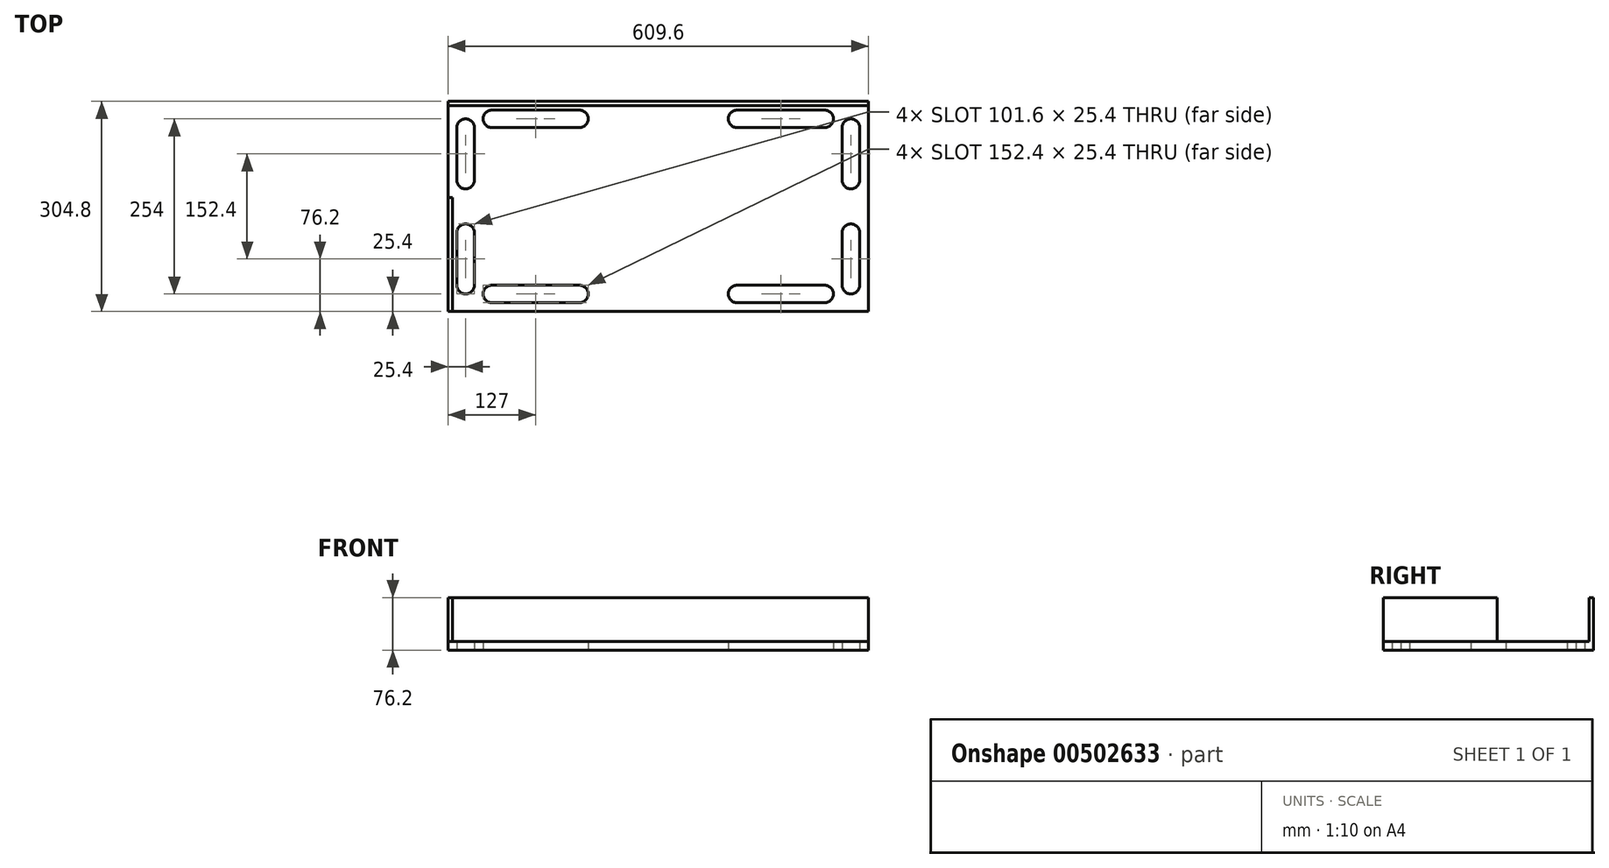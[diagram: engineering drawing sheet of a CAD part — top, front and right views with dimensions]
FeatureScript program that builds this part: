
annotation { "Feature Type Name" : "Feature", "Feature Type Description" : "" }
export const myFeature = defineFeature(function(context is Context, id is Id, definition is map)
    precondition{}
    {
        {
            var Q0;
            Q0=qCreatedBy(makeId("Top.planeOp"),FACE);
            var sketch = newSketch(context, id + "F0", { "sketchPlane" : qUnion([Q0])});
            skLineSegment(sketch, "E0.bottom", {"start": v(0, 0) * mm, "end": v(609.6, 0) * mm});
            skLineSegment(sketch, "E0.top", {"start": v(0, 304.8) * mm, "end": v(609.6, 304.8) * mm});
            skLineSegment(sketch, "E0.left", {"start": v(0, 0) * mm, "end": v(0, 304.8) * mm});
            skLineSegment(sketch, "E0.right", {"start": v(609.6, 0) * mm, "end": v(609.6, 304.8) * mm});
            skLineSegment(sketch, "E1", {"start": v(12.7, 190.5) * mm, "end": v(12.7, 266.7) * mm});
            skLineSegment(sketch, "E2", {"start": v(38.1, 190.5) * mm, "end": v(38.1, 266.7) * mm});
            skArc(sketch, "E3", {"start": v(12.7, 190.5) * mm, "mid": v(25.4, 177.8) * mm, "end": v(38.1, 190.5) * mm});
            skArc(sketch, "E4", {"start": v(38.1, 266.7) * mm, "mid": v(25.4, 279.4) * mm, "end": v(12.7, 266.7) * mm});
            skLineSegment(sketch, "E5", {"start": v(12.7, 38.1) * mm, "end": v(12.7, 114.3) * mm});
            skLineSegment(sketch, "E6", {"start": v(38.1, 38.1) * mm, "end": v(38.1, 114.3) * mm});
            skArc(sketch, "E7", {"start": v(12.7, 38.1) * mm, "mid": v(25.4, 25.4) * mm, "end": v(38.1, 38.1) * mm});
            skArc(sketch, "E8", {"start": v(38.1, 114.3) * mm, "mid": v(25.4, 127) * mm, "end": v(12.7, 114.3) * mm});
            skLineSegment(sketch, "E9", {"start": v(571.5, 190.5) * mm, "end": v(571.5, 266.7) * mm});
            skLineSegment(sketch, "E10", {"start": v(596.9, 190.5) * mm, "end": v(596.9, 266.7) * mm});
            skArc(sketch, "E11", {"start": v(571.5, 190.5) * mm, "mid": v(584.2, 177.8) * mm, "end": v(596.9, 190.5) * mm});
            skArc(sketch, "E12", {"start": v(596.9, 266.7) * mm, "mid": v(584.2, 279.4) * mm, "end": v(571.5, 266.7) * mm});
            skLineSegment(sketch, "E13", {"start": v(571.5, 38.1) * mm, "end": v(571.5, 114.3) * mm});
            skLineSegment(sketch, "E14", {"start": v(596.9, 38.1) * mm, "end": v(596.9, 114.3) * mm});
            skArc(sketch, "E15", {"start": v(571.5, 38.1) * mm, "mid": v(584.2, 25.4) * mm, "end": v(596.9, 38.1) * mm});
            skArc(sketch, "E16", {"start": v(596.9, 114.3) * mm, "mid": v(584.2, 127) * mm, "end": v(571.5, 114.3) * mm});
            skLineSegment(sketch, "E17", {"start": v(190.5, 12.7) * mm, "end": v(63.5, 12.7) * mm});
            skLineSegment(sketch, "E18", {"start": v(190.5, 38.1) * mm, "end": v(63.5, 38.1) * mm});
            skArc(sketch, "E19", {"start": v(190.5, 12.7) * mm, "mid": v(203.2, 25.4) * mm, "end": v(190.5, 38.1) * mm});
            skArc(sketch, "E20", {"start": v(63.5, 38.1) * mm, "mid": v(50.8, 25.4) * mm, "end": v(63.5, 12.7) * mm});
            skLineSegment(sketch, "E21", {"start": v(546.1, 12.7) * mm, "end": v(419.1, 12.7) * mm});
            skLineSegment(sketch, "E22", {"start": v(546.1, 38.1) * mm, "end": v(419.1, 38.1) * mm});
            skArc(sketch, "E23", {"start": v(546.1, 12.7) * mm, "mid": v(558.8, 25.4) * mm, "end": v(546.1, 38.1) * mm});
            skArc(sketch, "E24", {"start": v(419.1, 38.1) * mm, "mid": v(406.4, 25.4) * mm, "end": v(419.1, 12.7) * mm});
            skLineSegment(sketch, "E25", {"start": v(190.5, 266.7) * mm, "end": v(63.5, 266.7) * mm});
            skLineSegment(sketch, "E26", {"start": v(190.5, 292.1) * mm, "end": v(63.5, 292.1) * mm});
            skArc(sketch, "E27", {"start": v(190.5, 266.7) * mm, "mid": v(203.2, 279.4) * mm, "end": v(190.5, 292.1) * mm});
            skArc(sketch, "E28", {"start": v(63.5, 292.1) * mm, "mid": v(50.8, 279.4) * mm, "end": v(63.5, 266.7) * mm});
            skLineSegment(sketch, "E29", {"start": v(546.1, 266.7) * mm, "end": v(419.1, 266.7) * mm});
            skLineSegment(sketch, "E30", {"start": v(546.1, 292.1) * mm, "end": v(419.1, 292.1) * mm});
            skArc(sketch, "E31", {"start": v(546.1, 266.7) * mm, "mid": v(558.8, 279.4) * mm, "end": v(546.1, 292.1) * mm});
            skArc(sketch, "E32", {"start": v(419.1, 292.1) * mm, "mid": v(406.4, 279.4) * mm, "end": v(419.1, 266.7) * mm});
            skSolve(sketch);
        }
        {
            var Q0;
            Q0=makeQuery(id+"F0.imprint","IMPRINT",FACE,{"disambiguationData":[TD([[makeQuery(id+"F0.imprint","IMPRINT",EDGE,{"derivedFrom":sQuery(id+"F0.wireOp",EDGE,"E0.bottom")}),1.0]])]});
            extrude(context, id + "F1", {"entities" : qUnion([Q0]), "depth" : 12.7 * mm});
        }
        {
            var Q0;
            Q0=makeQuery(id+"F1.opExtrude","SWEPT_FACE",FACE,{"disambiguationData":[OSD([sQuery(id+"F0.wireOp",EDGE,"E0.top")])]});
            var sketch = newSketch(context, id + "F2", { "sketchPlane" : qUnion([Q0])});
            skLineSegment(sketch, "E33.bottom", {"start": v(-609.6, 0) * mm, "end": v(0, 0) * mm});
            skLineSegment(sketch, "E33.top", {"start": v(-609.6, 76.2) * mm, "end": v(0, 76.2) * mm});
            skLineSegment(sketch, "E33.left", {"start": v(-609.6, 0) * mm, "end": v(-609.6, 76.2) * mm});
            skLineSegment(sketch, "E33.right", {"start": v(0, 0) * mm, "end": v(0, 76.2) * mm});
            skSolve(sketch);
        }
        {
            var Q0;
            {var subQ0=sQuery(id+"F2.wireOp",EDGE,"E33.top");Q0=makeQuery(id+"F2.imprint","IMPRINT",FACE,{"disambiguationData":[TD([[makeQuery(id+"F2.imprint","IMPRINT",EDGE,{"derivedFrom":subQ0}),-1.0]])]});}
            extrude(context, id + "F3", {"entities" : qUnion([Q0]), "operationType" : NewBodyOperationType.ADD, "oppositeDirection" : true, "depth" : 6.35 * mm});
        }
        {
            var Q0;
            Q0=makeQuery(id+"F3.boolean.opBoolean","MERGE",FACE,{"derivedFrom":[makeQuery(id+"F1.opExtrude","SWEPT_FACE",FACE,{"disambiguationData":[OSD([sQuery(id+"F0.wireOp",EDGE,"E0.left")])]}),makeQuery(id+"F3.opExtrude","SWEPT_FACE",FACE,{"disambiguationData":[OSD([sQuery(id+"F2.wireOp",EDGE,"E33.right")])]})]});
            var sketch = newSketch(context, id + "F4", { "sketchPlane" : qUnion([Q0])});
            skLineSegment(sketch, "E34.bottom", {"start": v(0, 0) * mm, "end": v(-165.1, 0) * mm});
            skLineSegment(sketch, "E34.top", {"start": v(0, 76.2) * mm, "end": v(-165.1, 76.2) * mm});
            skLineSegment(sketch, "E34.left", {"start": v(0, 0) * mm, "end": v(0, 76.2) * mm});
            skLineSegment(sketch, "E34.right", {"start": v(-165.1, 0) * mm, "end": v(-165.1, 76.2) * mm});
            skSolve(sketch);
        }
        {
            var Q0;
            {var subQ0=sQuery(id+"F4.wireOp",EDGE,"E34.top");Q0=makeQuery(id+"F4.imprint","IMPRINT",FACE,{"disambiguationData":[TD([[makeQuery(id+"F4.imprint","IMPRINT",EDGE,{"derivedFrom":subQ0}),1.0]])]});}
            extrude(context, id + "F5", {"entities" : qUnion([Q0]), "oppositeDirection" : true, "depth" : 6.35 * mm});
        }
    });
